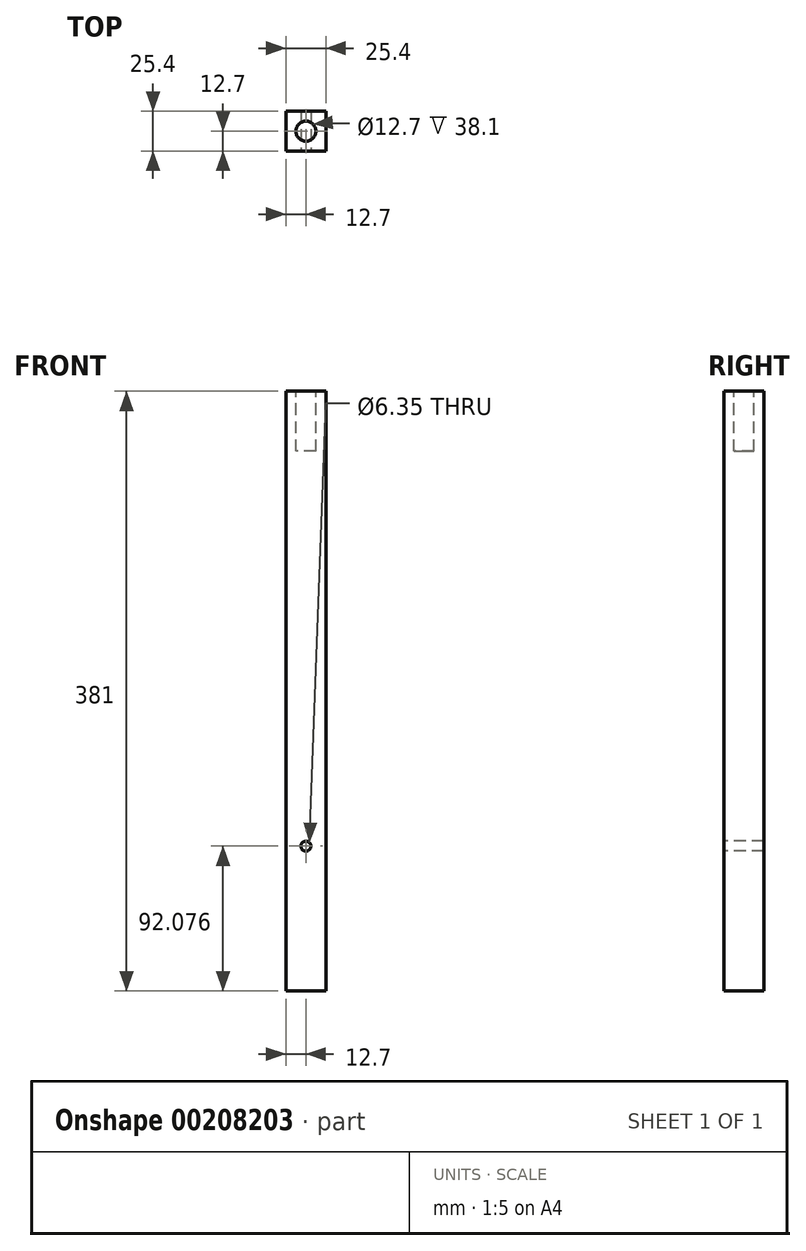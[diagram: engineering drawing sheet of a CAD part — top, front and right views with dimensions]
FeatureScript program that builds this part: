
annotation { "Feature Type Name" : "Feature", "Feature Type Description" : "" }
export const myFeature = defineFeature(function(context is Context, id is Id, definition is map)
    precondition{}
    {
        {
            var Q0;
            Q0=qCreatedBy(makeId("Front.planeOp"),FACE);
            var sketch = newSketch(context, id + "F0", { "sketchPlane" : qUnion([Q0])});
            skLineSegment(sketch, "E0.bottom", {"start": v(-12.7, 190.5) * mm, "end": v(12.7, 190.5) * mm});
            skLineSegment(sketch, "E0.top", {"start": v(-12.7, -190.5) * mm, "end": v(12.7, -190.5) * mm});
            skLineSegment(sketch, "E0.left", {"start": v(-12.7, 190.5) * mm, "end": v(-12.7, -190.5) * mm});
            skLineSegment(sketch, "E0.right", {"start": v(12.7, 190.5) * mm, "end": v(12.7, -190.5) * mm});
            skPoint(sketch, "E0.middle", {"position": v(0, 0) * mm});
            skSolve(sketch);
        }
        {
            var Q0;
            Q0 = qSketchRegion(id + "F0", true);
            extrude(context, id + "F1", {"entities" : qUnion([Q0]), "depth" : 25.4 * mm});
        }
        {
            var Q0;
            Q0=makeQuery(id+"F1.opExtrude","SWEPT_FACE",FACE,{"disambiguationData":[OSD([sQuery(id+"F0.wireOp",EDGE,"E0.bottom")])]});
            var sketch = newSketch(context, id + "F2", { "sketchPlane" : qUnion([Q0])});
            skLineSegment(sketch, "E1", {"start": v(-12.7, 0) * mm, "end": v(12.7, -25.4) * mm, "construction": true});
            skLineSegment(sketch, "E2", {"start": v(-12.7, -25.4) * mm, "end": v(12.7, 0) * mm, "construction": true});
            skCircle(sketch, "E3", {"center": v(0, -12.7) * mm, "radius": 6.35 * mm});
            skSolve(sketch);
        }
        {
            var Q0;
            Q0 = qSketchRegion(id + "F2", true);
            extrude(context, id + "F3", {"entities" : qUnion([Q0]), "operationType" : NewBodyOperationType.REMOVE, "oppositeDirection" : true, "depth" : 38.1 * mm});
        }
        {
            var Q0;
            Q0=makeQuery(id+"F1.opExtrude","CAP_FACE",FACE,{"disambiguationData":[OSD([sQuery(id+"F0.wireOp",EDGE,"E0.bottom"),sQuery(id+"F0.wireOp",EDGE,"E0.top"),sQuery(id+"F0.wireOp",EDGE,"E0.left"),sQuery(id+"F0.wireOp",EDGE,"E0.right")])],"isStart":false});
            var sketch = newSketch(context, id + "F4", { "sketchPlane" : qUnion([Q0])});
            skLineSegment(sketch, "E4", {"start": v(0, -190.5) * mm, "end": v(0, -82.55) * mm, "construction": true});
            skPoint(sketch, "E4.endSnap0", {"position": v(0, -190.5) * mm});
            skLineSegment(sketch, "E5", {"start": v(0, -190.5) * mm, "end": v(0, -88.9) * mm});
            skCircle(sketch, "E6", {"center": v(0, -98.42) * mm, "radius": 3.18 * mm});
            skLineSegment(sketch, "E7", {"start": v(0, -98.42) * mm, "end": v(0, -73.02) * mm, "construction": true});
            skSolve(sketch);
        }
        {
            var Q0;
            Q0 = qSketchRegion(id + "F4", true);
            extrude(context, id + "F5", {"entities" : qUnion([Q0]), "operationType" : NewBodyOperationType.REMOVE, "endBound" : BoundingType.THROUGH_ALL, "oppositeDirection" : true, "depth" : 25.4 * mm});
        }
    });
